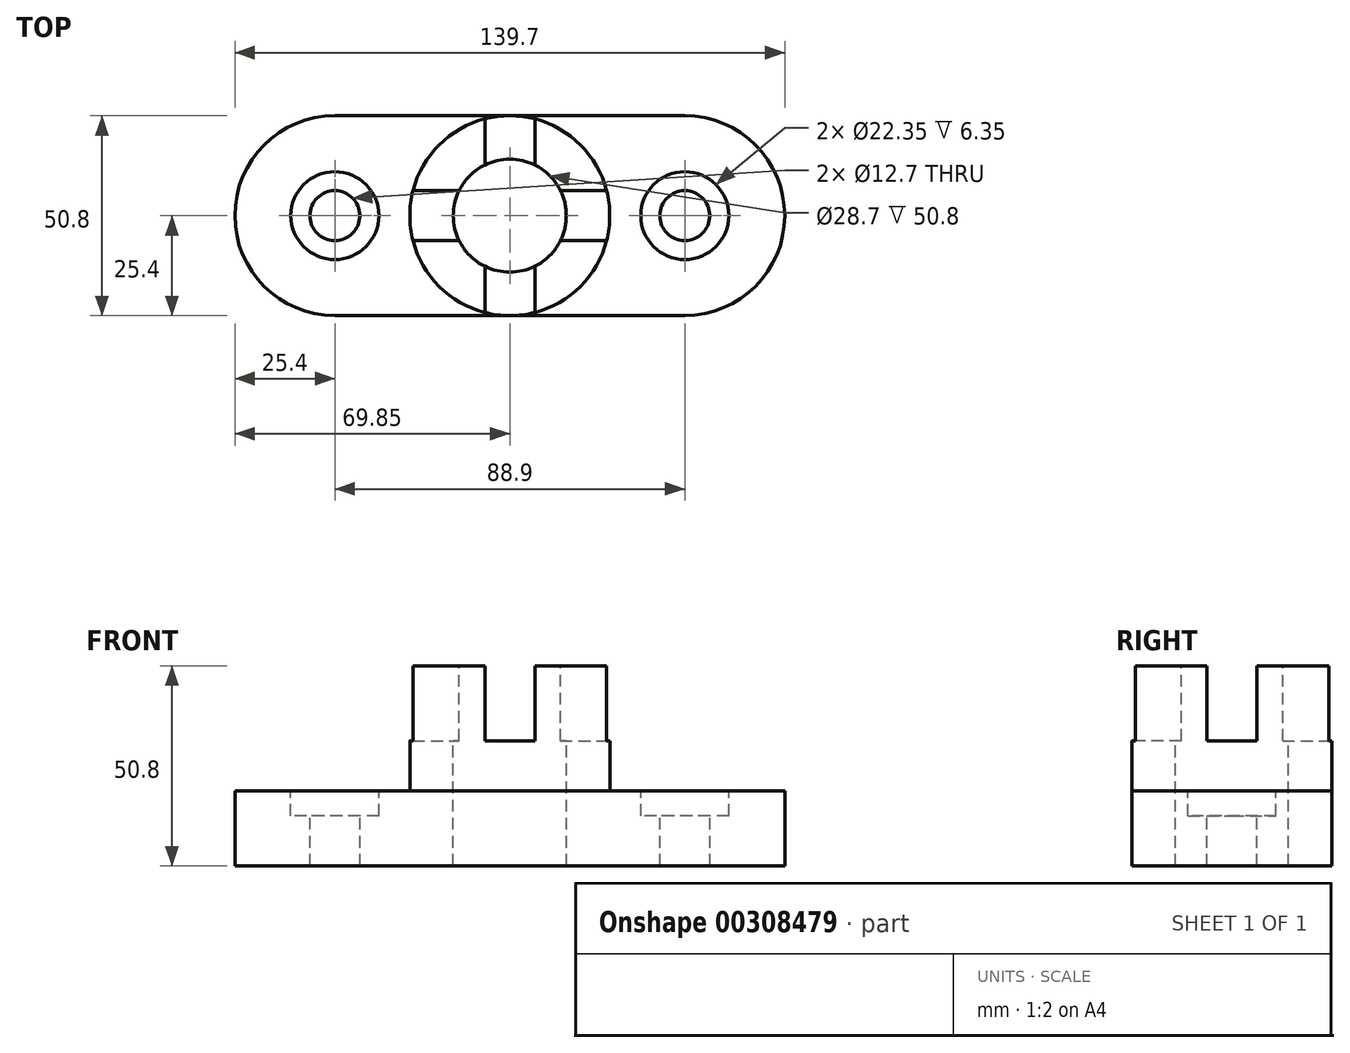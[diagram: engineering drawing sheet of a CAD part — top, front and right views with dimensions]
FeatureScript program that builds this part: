
annotation { "Feature Type Name" : "Feature", "Feature Type Description" : "" }
export const myFeature = defineFeature(function(context is Context, id is Id, definition is map)
    precondition{}
    {
        {
            var Q0;
            Q0=qCreatedBy(makeId("Top.planeOp"),FACE);
            var sketch = newSketch(context, id + "F0", { "sketchPlane" : qUnion([Q0])});
            skLineSegment(sketch, "E0", {"start": v(-44.45, 0) * mm, "end": v(44.45, 0) * mm, "construction": true});
            skArc(sketch, "E1", {"start": v(-44.45, 25.4) * mm, "mid": v(-69.85, 0) * mm, "end": v(-44.45, -25.4) * mm});
            skArc(sketch, "E2", {"start": v(44.45, -25.4) * mm, "mid": v(69.85, 0) * mm, "end": v(44.45, 25.4) * mm});
            skLineSegment(sketch, "E3", {"start": v(-44.45, 25.4) * mm, "end": v(44.45, 25.4) * mm});
            skLineSegment(sketch, "E4", {"start": v(-44.45, -25.4) * mm, "end": v(44.45, -25.4) * mm});
            skLineSegment(sketch, "E5", {"start": v(-44.45, 25.4) * mm, "end": v(-44.45, -25.4) * mm, "construction": true});
            skLineSegment(sketch, "E6", {"start": v(44.45, 25.4) * mm, "end": v(44.45, -25.4) * mm, "construction": true});
            skSolve(sketch);
        }
        {
            var Q0;
            Q0 = qSketchRegion(id + "F0", true);
            extrude(context, id + "F1", {"entities" : qUnion([Q0]), "depth" : 19.05 * mm});
        }
        {
            var Q0;
            Q0=makeQuery(id+"F1.opExtrude","CAP_FACE",FACE,{"disambiguationData":[OSD([sQuery(id+"F0.wireOp",EDGE,"E1"),sQuery(id+"F0.wireOp",EDGE,"E2"),sQuery(id+"F0.wireOp",EDGE,"E3"),sQuery(id+"F0.wireOp",EDGE,"E4")])],"isStart":false});
            var sketch = newSketch(context, id + "F2", { "sketchPlane" : qUnion([Q0])});
            skLineSegment(sketch, "E7", {"start": v(-44.45, 0) * mm, "end": v(44.45, 0) * mm, "construction": true});
            skCircle(sketch, "E8", {"center": v(-44.45, 0) * mm, "radius": 11.18 * mm});
            skCircle(sketch, "E9", {"center": v(44.45, 0) * mm, "radius": 11.18 * mm});
            skSolve(sketch);
        }
        {
            var Q0;
            Q0 = qSketchRegion(id + "F2", true);
            extrude(context, id + "F3", {"entities" : qUnion([Q0]), "operationType" : NewBodyOperationType.REMOVE, "oppositeDirection" : true, "depth" : 6.35 * mm});
        }
        {
            var Q0;
            Q0=makeQuery(id+"F1.opExtrude","CAP_FACE",FACE,{"disambiguationData":[OSD([sQuery(id+"F0.wireOp",EDGE,"E1"),sQuery(id+"F0.wireOp",EDGE,"E2"),sQuery(id+"F0.wireOp",EDGE,"E3"),sQuery(id+"F0.wireOp",EDGE,"E4")])],"isStart":false});
            var sketch = newSketch(context, id + "F4", { "sketchPlane" : qUnion([Q0])});
            skLineSegment(sketch, "E10", {"start": v(-44.45, 0) * mm, "end": v(44.45, 0) * mm, "construction": true});
            skCircle(sketch, "E11", {"center": v(-44.45, 0) * mm, "radius": 6.35 * mm});
            skCircle(sketch, "E12", {"center": v(44.45, 0) * mm, "radius": 6.35 * mm});
            skSolve(sketch);
        }
        {
            var Q0;
            Q0 = qSketchRegion(id + "F4", true);
            extrude(context, id + "F5", {"entities" : qUnion([Q0]), "operationType" : NewBodyOperationType.REMOVE, "endBound" : BoundingType.THROUGH_ALL, "oppositeDirection" : true, "depth" : 25.4 * mm});
        }
        {
            var Q0;
            Q0=makeQuery(id+"F1.opExtrude","CAP_FACE",FACE,{"disambiguationData":[OSD([sQuery(id+"F0.wireOp",EDGE,"E1"),sQuery(id+"F0.wireOp",EDGE,"E2"),sQuery(id+"F0.wireOp",EDGE,"E3"),sQuery(id+"F0.wireOp",EDGE,"E4")])],"isStart":false});
            var sketch = newSketch(context, id + "F6", { "sketchPlane" : qUnion([Q0])});
            skCircle(sketch, "E13", {"center": v(0, 0) * mm, "radius": 25.4 * mm});
            skSolve(sketch);
        }
        {
            var Q0;
            Q0 = qSketchRegion(id + "F6", true);
            extrude(context, id + "F7", {"entities" : qUnion([Q0]), "operationType" : NewBodyOperationType.ADD, "depth" : 31.75 * mm});
        }
        {
            var Q0;
            Q0=makeQuery(id+"F7.opExtrude","CAP_FACE",FACE,{"disambiguationData":[OSD([sQuery(id+"F6.wireOp",EDGE,"E13")])],"isStart":false});
            var sketch = newSketch(context, id + "F8", { "sketchPlane" : qUnion([Q0])});
            skCircle(sketch, "E14", {"center": v(0, 0) * mm, "radius": 14.35 * mm});
            skSolve(sketch);
        }
        {
            var Q0;
            Q0 = qSketchRegion(id + "F8", true);
            extrude(context, id + "F9", {"entities" : qUnion([Q0]), "operationType" : NewBodyOperationType.REMOVE, "endBound" : BoundingType.THROUGH_ALL, "oppositeDirection" : true, "depth" : 25.4 * mm});
        }
        {
            var Q0;
            Q0=makeQuery(id+"F7.opExtrude","CAP_FACE",FACE,{"disambiguationData":[OSD([sQuery(id+"F6.wireOp",EDGE,"E13")])],"isStart":false});
            var sketch = newSketch(context, id + "F10", { "sketchPlane" : qUnion([Q0])});
            skLineSegment(sketch, "E15", {"start": v(-25.4, 25.4) * mm, "end": v(-25.4, -25.4) * mm, "construction": true});
            skLineSegment(sketch, "E16", {"start": v(-25.4, -25.4) * mm, "end": v(25.4, -25.4) * mm, "construction": true});
            skLineSegment(sketch, "E17", {"start": v(25.4, -25.4) * mm, "end": v(25.4, 25.4) * mm, "construction": true});
            skLineSegment(sketch, "E18", {"start": v(25.4, 25.4) * mm, "end": v(-25.4, 25.4) * mm, "construction": true});
            skPoint(sketch, "E19", {"position": v(-25.4, 6.35) * mm});
            skPoint(sketch, "E20", {"position": v(-25.4, -6.35) * mm});
            skPoint(sketch, "E21", {"position": v(25.4, 6.35) * mm});
            skPoint(sketch, "E22", {"position": v(25.4, -6.35) * mm});
            skPoint(sketch, "E23", {"position": v(6.35, -25.4) * mm});
            skPoint(sketch, "E24", {"position": v(-6.35, -25.4) * mm});
            skPoint(sketch, "E25", {"position": v(-6.35, 25.4) * mm});
            skPoint(sketch, "E26", {"position": v(6.35, 25.4) * mm});
            skLineSegment(sketch, "E27", {"start": v(-25.4, 6.35) * mm, "end": v(0, 0) * mm, "construction": true});
            skLineSegment(sketch, "E28", {"start": v(0, 0) * mm, "end": v(-25.4, -6.35) * mm, "construction": true});
            skLineSegment(sketch, "E29", {"start": v(-6.35, 25.4) * mm, "end": v(0, 0) * mm, "construction": true});
            skLineSegment(sketch, "E30", {"start": v(6.35, 25.4) * mm, "end": v(0, 0) * mm, "construction": true});
            skLineSegment(sketch, "E31", {"start": v(25.4, 6.35) * mm, "end": v(0, 0) * mm, "construction": true});
            skLineSegment(sketch, "E32", {"start": v(6.35, -25.4) * mm, "end": v(0, 0) * mm, "construction": true});
            skLineSegment(sketch, "E33", {"start": v(-6.35, -25.4) * mm, "end": v(0, 0) * mm, "construction": true});
            skLineSegment(sketch, "E34", {"start": v(-25.4, 6.35) * mm, "end": v(25.4, 6.35) * mm});
            skLineSegment(sketch, "E35", {"start": v(25.4, -6.35) * mm, "end": v(-25.4, -6.35) * mm});
            skLineSegment(sketch, "E36", {"start": v(-6.35, 25.4) * mm, "end": v(-6.35, -25.4) * mm});
            skLineSegment(sketch, "E37", {"start": v(6.35, -25.4) * mm, "end": v(6.35, 25.4) * mm});
            skSolve(sketch);
        }
        {
            var Q0;
            Q0 = qSketchRegion(id + "F10", true);
            var Q1;
            {var subQ0=sQuery(id+"F10.wireOp",EDGE,"E34");var subQ1=makeQuery(id+"F7.opExtrude","CAP_EDGE",EDGE,{"disambiguationData":[OSD([sQuery(id+"F6.wireOp",EDGE,"E13")])],"isStart":false});var subQ2=makeQuery(id+"F10.imprint","INTERSECT",VERTEX,{"disambiguationData":[OD(0.0)],"derivedFrom":[subQ1,subQ0]});Q1=makeQuery(id+"F10.imprint","IMPRINT",FACE,{"disambiguationData":[TD([[makeQuery(id+"F10.imprint","IMPRINT",EDGE,{"disambiguationData":[TD([[subQ2,-1.0]])],"derivedFrom":subQ0}),-1.0]])]});}
            var Q2;
            {var subQ0=sQuery(id+"F10.wireOp",EDGE,"E34");var subQ1=makeQuery(id+"F7.opExtrude","CAP_EDGE",EDGE,{"disambiguationData":[OSD([sQuery(id+"F6.wireOp",EDGE,"E13")])],"isStart":false});var subQ2=makeQuery(id+"F10.imprint","INTERSECT",VERTEX,{"disambiguationData":[OD(1.0)],"derivedFrom":[subQ1,subQ0]});Q2=makeQuery(id+"F10.imprint","IMPRINT",FACE,{"disambiguationData":[TD([[makeQuery(id+"F10.imprint","IMPRINT",EDGE,{"disambiguationData":[TD([[subQ2,1.0]])],"derivedFrom":subQ0}),-1.0]])]});}
            var Q3;
            {var subQ0=sQuery(id+"F10.wireOp",EDGE,"E34");var subQ1=makeQuery(id+"F9.boolean.opBoolean","COPY",EDGE,{"derivedFrom":makeQuery(id+"F9.opExtrude","CAP_EDGE",EDGE,{"disambiguationData":[OSD([sQuery(id+"F8.wireOp",EDGE,"E14")])],"isStart":true})});var subQ2=makeQuery(id+"F10.imprint","INTERSECT",VERTEX,{"disambiguationData":[OD(0.0)],"derivedFrom":[subQ1,subQ0]});Q3=makeQuery(id+"F10.imprint","IMPRINT",FACE,{"disambiguationData":[TD([[makeQuery(id+"F10.imprint","IMPRINT",EDGE,{"disambiguationData":[TD([[subQ2,-1.0]])],"derivedFrom":subQ0}),-1.0]])]});}
            extrude(context, id + "F11", {"entities" : qUnion([Q0, Q1, Q2, Q3]), "operationType" : NewBodyOperationType.REMOVE, "oppositeDirection" : true, "depth" : 19.05 * mm});
        }
        {
            var Q0;
            {var subQ0=sQuery(id+"F10.wireOp",EDGE,"E36");var subQ1=makeQuery(id+"F7.opExtrude","CAP_EDGE",EDGE,{"disambiguationData":[OSD([sQuery(id+"F6.wireOp",EDGE,"E13")])],"isStart":false});var subQ2=makeQuery(id+"F10.imprint","INTERSECT",VERTEX,{"disambiguationData":[OD(0.0)],"derivedFrom":[subQ1,subQ0]});Q0=makeQuery(id+"F10.imprint","IMPRINT",FACE,{"disambiguationData":[TD([[makeQuery(id+"F10.imprint","IMPRINT",EDGE,{"disambiguationData":[TD([[subQ2,-1.0]])],"derivedFrom":subQ0}),1.0]])]});}
            var Q1;
            {var subQ0=sQuery(id+"F10.wireOp",EDGE,"E36");var subQ1=sQuery(id+"F10.wireOp",EDGE,"E34");var subQ2=makeQuery(id+"F10.imprint","INTERSECT",VERTEX,{"derivedFrom":[subQ1,subQ0]});Q1=makeQuery(id+"F10.imprint","IMPRINT",FACE,{"disambiguationData":[TD([[makeQuery(id+"F10.imprint","IMPRINT",EDGE,{"disambiguationData":[TD([[subQ2,-1.0]])],"derivedFrom":subQ1}),1.0]])]});}
            var Q2;
            {var subQ0=sQuery(id+"F10.wireOp",EDGE,"E36");var subQ1=sQuery(id+"F10.wireOp",EDGE,"E34");var subQ2=makeQuery(id+"F10.imprint","INTERSECT",VERTEX,{"derivedFrom":[subQ1,subQ0]});Q2=makeQuery(id+"F10.imprint","IMPRINT",FACE,{"disambiguationData":[TD([[makeQuery(id+"F10.imprint","IMPRINT",EDGE,{"disambiguationData":[TD([[subQ2,-1.0]])],"derivedFrom":subQ1}),-1.0]])]});}
            var Q3;
            {var subQ0=sQuery(id+"F10.wireOp",EDGE,"E37");var subQ1=sQuery(id+"F10.wireOp",EDGE,"E35");var subQ2=makeQuery(id+"F10.imprint","INTERSECT",VERTEX,{"derivedFrom":[subQ1,subQ0]});Q3=makeQuery(id+"F10.imprint","IMPRINT",FACE,{"disambiguationData":[TD([[makeQuery(id+"F10.imprint","IMPRINT",EDGE,{"disambiguationData":[TD([[subQ2,-1.0]])],"derivedFrom":subQ1}),1.0]])]});}
            var Q4;
            {var subQ0=sQuery(id+"F10.wireOp",EDGE,"E36");var subQ1=makeQuery(id+"F7.opExtrude","CAP_EDGE",EDGE,{"disambiguationData":[OSD([sQuery(id+"F6.wireOp",EDGE,"E13")])],"isStart":false});var subQ2=makeQuery(id+"F10.imprint","INTERSECT",VERTEX,{"disambiguationData":[OD(1.0)],"derivedFrom":[subQ1,subQ0]});Q4=makeQuery(id+"F10.imprint","IMPRINT",FACE,{"disambiguationData":[TD([[makeQuery(id+"F10.imprint","IMPRINT",EDGE,{"disambiguationData":[TD([[subQ2,1.0]])],"derivedFrom":subQ0}),1.0]])]});}
            extrude(context, id + "F12", {"entities" : qUnion([Q0, Q1, Q2, Q3, Q4]), "operationType" : NewBodyOperationType.REMOVE, "oppositeDirection" : true, "depth" : 19.05 * mm});
        }
    });
